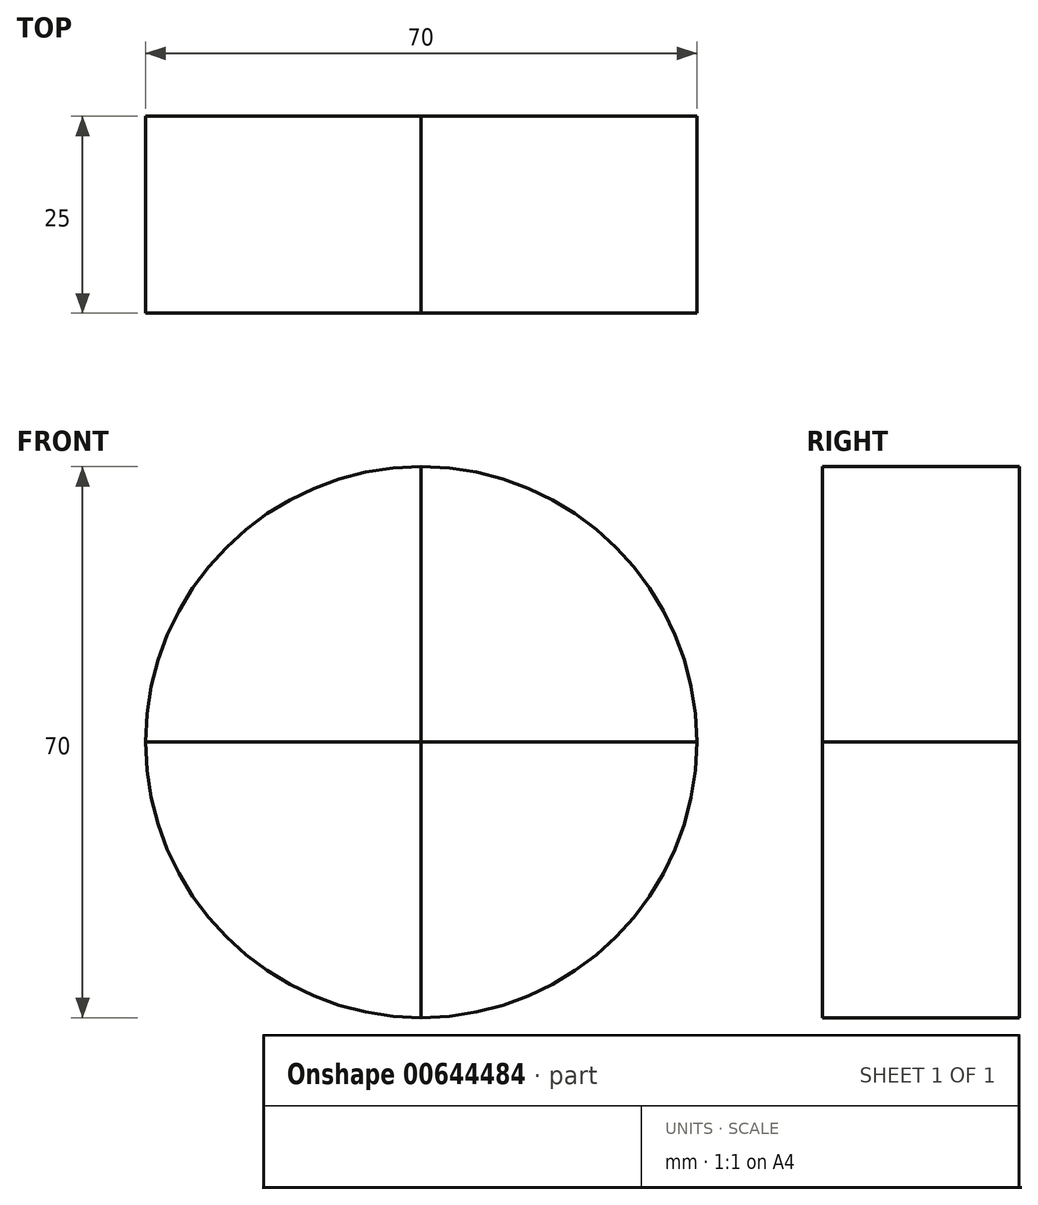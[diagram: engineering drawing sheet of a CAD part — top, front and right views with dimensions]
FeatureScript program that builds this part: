
annotation { "Feature Type Name" : "Feature", "Feature Type Description" : "" }
export const myFeature = defineFeature(function(context is Context, id is Id, definition is map)
    precondition{}
    {
        {
            var Q0;
            Q0=qCreatedBy(makeId("Front.planeOp"),FACE);
            var sketch = newSketch(context, id + "F0", { "sketchPlane" : qUnion([Q0])});
            skCircle(sketch, "E0", {"center": v(0, 0) * mm, "radius": 35 * mm});
            skLineSegment(sketch, "E1", {"start": v(0, 35) * mm, "end": v(0, -35) * mm});
            skLineSegment(sketch, "E2", {"start": v(-35, 0) * mm, "end": v(35, 0) * mm});
            skSolve(sketch);
        }
        {
            var Q0;
            {var subQ0=sQuery(id+"F0.wireOp",EDGE,"E1");var subQ1=sQuery(id+"F0.wireOp",EDGE,"E0");var subQ2=makeQuery(id+"F0.imprint","INTERSECT",VERTEX,{"disambiguationData":[OD(0.0)],"derivedFrom":[subQ1,subQ0]});Q0=makeQuery(id+"F0.imprint","IMPRINT",FACE,{"disambiguationData":[TD([[makeQuery(id+"F0.imprint","IMPRINT",EDGE,{"disambiguationData":[TD([[subQ2,-1.0]])],"derivedFrom":subQ1}),1.0]])]});}
            extrude(context, id + "F1", {"entities" : qUnion([Q0]), "depth" : 25 * mm, "offsetDistance" : 25 * mm});
        }
        {
            var Q0;
            Q0=makeQuery(id+"F1.opExtrude","SWEPT_BODY",BODY,{"disambiguationData":[OSD([sQuery(id+"F0.wireOp",EDGE,"E0"),sQuery(id+"F0.wireOp",EDGE,"E1"),sQuery(id+"F0.wireOp",EDGE,"E2")])]});
            var Q1;
            Q1=makeQuery(id+"F1.opExtrude","SWEPT_EDGE",EDGE,{"disambiguationData":[OSD([sQuery(id+"F0.wireOp",EDGE,"E1"),sQuery(id+"F0.wireOp",EDGE,"E2")])]});
            circularPattern(context, id + "F2", {"entities" : qUnion([Q0]), "axis" : qUnion([Q1]), "angle" : 360 * degree, "instanceCount" : 4, "equalSpace" : true});
        }
    });
